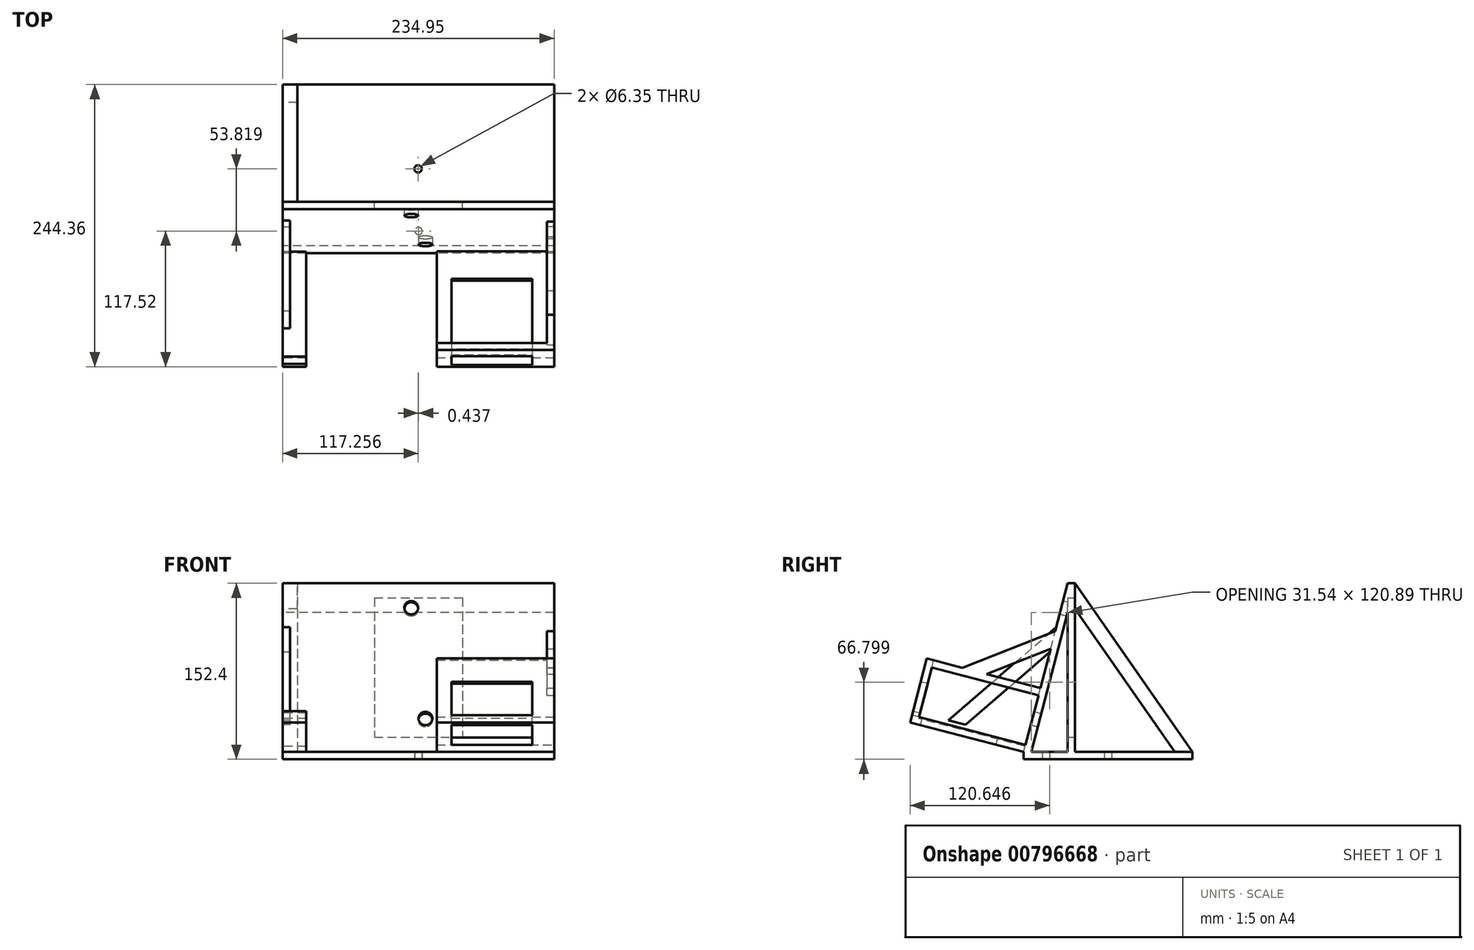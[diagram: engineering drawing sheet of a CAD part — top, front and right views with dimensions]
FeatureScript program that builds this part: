
annotation { "Feature Type Name" : "Feature", "Feature Type Description" : "" }
export const myFeature = defineFeature(function(context is Context, id is Id, definition is map)
    precondition{}
    {
        {
            var Q0;
            Q0=qCreatedBy(makeId("Right.planeOp"),FACE);
            var sketch = newSketch(context, id + "F0", { "sketchPlane" : qUnion([Q0])});
            skLineSegment(sketch, "E0.bottom", {"start": v(-30.3, 47.63) * mm, "end": v(14.14, 47.63) * mm, "construction": true});
            skLineSegment(sketch, "E0.top", {"start": v(-30.3, 41.28) * mm, "end": v(14.14, 41.28) * mm});
            skLineSegment(sketch, "E0.left", {"start": v(-30.3, 47.63) * mm, "end": v(-30.3, 41.28) * mm});
            skLineSegment(sketch, "E0.right", {"start": v(14.14, 47.63) * mm, "end": v(14.14, 41.28) * mm});
            skLineSegment(sketch, "E1.bottom", {"start": v(14.14, 47.63) * mm, "end": v(7.8, 47.63) * mm});
            skLineSegment(sketch, "E1.top", {"start": v(14.14, 193.68) * mm, "end": v(7.8, 193.68) * mm});
            skLineSegment(sketch, "E1.left", {"start": v(14.14, 47.63) * mm, "end": v(14.14, 193.68) * mm});
            skLineSegment(sketch, "E1.right", {"start": v(7.8, 47.63) * mm, "end": v(7.8, 193.68) * mm});
            skLineSegment(sketch, "E2.bottom", {"start": v(14.14, 41.28) * mm, "end": v(115.74, 41.28) * mm});
            skLineSegment(sketch, "E2.top", {"start": v(14.14, 47.63) * mm, "end": v(115.74, 47.63) * mm});
            skLineSegment(sketch, "E2.left", {"start": v(14.14, 41.28) * mm, "end": v(14.14, 47.63) * mm});
            skLineSegment(sketch, "E2.right", {"start": v(115.74, 41.28) * mm, "end": v(115.74, 47.63) * mm});
            skLineSegment(sketch, "E3", {"start": v(-30.3, 47.63) * mm, "end": v(7.8, 193.68) * mm});
            skLineSegment(sketch, "E4", {"start": v(-23.72, 47.63) * mm, "end": v(7.8, 168.45) * mm, "construction": true});
            skLineSegment(sketch, "E5", {"start": v(-17.69, 96) * mm, "end": v(-11.54, 94.4) * mm, "construction": true});
            skLineSegment(sketch, "E6", {"start": v(-23.72, 47.63) * mm, "end": v(7.8, 47.63) * mm, "construction": true});
            skLineSegment(sketch, "E7", {"start": v(7.8, 47.63) * mm, "end": v(7.8, 168.45) * mm, "construction": true});
            skLineSegment(sketch, "E8", {"start": v(115.74, 47.63) * mm, "end": v(115.74, 94.76) * mm, "construction": true});
            skSolve(sketch);
        }
        {
            var Q0;
            Q0=makeQuery(id+"F0.imprint","IMPRINT",FACE,{"disambiguationData":[TD([[makeQuery(id+"F0.imprint","IMPRINT",EDGE,{"derivedFrom":sQuery(id+"F0.wireOp",EDGE,"E0.top")}),1.0]])]});
            var Q1;
            {var subQ1=sQuery(id+"F0.wireOp",EDGE,"E1.bottom");Q1=makeQuery(id+"F0.imprint","IMPRINT",FACE,{"disambiguationData":[TD([[makeQuery(id+"F0.imprint","IMPRINT",EDGE,{"derivedFrom":subQ1}),-1.0]])]});}
            var Q2;
            {var subQ0=sQuery(id+"F0.wireOp",EDGE,"E3");Q2=makeQuery(id+"F0.imprint","IMPRINT",FACE,{"disambiguationData":[TD([[makeQuery(id+"F0.imprint","IMPRINT",EDGE,{"derivedFrom":subQ0}),-1.0]])]});}
            var Q3;
            Q3=makeQuery(id+"F0.imprint","IMPRINT",FACE,{"disambiguationData":[TD([[makeQuery(id+"F0.imprint","IMPRINT",EDGE,{"derivedFrom":sQuery(id+"F0.wireOp",EDGE,"E2.bottom")}),1.0]])]});
            extrude(context, id + "F1", {"entities" : qUnion([Q0, Q1, Q2, Q3]), "depth" : 228.6 * mm, "offsetDistance" : 25.4 * mm});
        }
        {
            var Q0;
            Q0=makeQuery(id+"F1.opExtrude","CAP_FACE",FACE,{"disambiguationData":[OSD([sQuery(id+"F0.wireOp",EDGE,"E0.bottom"),sQuery(id+"F0.wireOp",EDGE,"E0.top"),sQuery(id+"F0.wireOp",EDGE,"E0.left"),sQuery(id+"F0.wireOp",EDGE,"E1.top"),sQuery(id+"F0.wireOp",EDGE,"E1.left"),sQuery(id+"F0.wireOp",EDGE,"E1.right"),sQuery(id+"F0.wireOp",EDGE,"E2.bottom"),sQuery(id+"F0.wireOp",EDGE,"E2.top"),sQuery(id+"F0.wireOp",EDGE,"E2.right"),sQuery(id+"F0.wireOp",EDGE,"E3"),sQuery(id+"F0.wireOp",EDGE,"E4")])],"isStart":false});
            var sketch = newSketch(context, id + "F2", { "sketchPlane" : qUnion([Q0])});
            skLineSegment(sketch, "E9", {"start": v(-30.3, 47.63) * mm, "end": v(-128.62, 73.28) * mm});
            skLineSegment(sketch, "E10", {"start": v(-128.62, 73.28) * mm, "end": v(-114.19, 128.58) * mm});
            skLineSegment(sketch, "E11", {"start": v(-114.19, 128.58) * mm, "end": v(-15.88, 102.93) * mm, "construction": true});
            skLineSegment(sketch, "E12", {"start": v(-121.4, 100.93) * mm, "end": v(-115.26, 99.32) * mm, "construction": true});
            skLineSegment(sketch, "E13", {"start": v(-67.67, 116.44) * mm, "end": v(-69.28, 110.3) * mm, "construction": true});
            skLineSegment(sketch, "E14", {"start": v(-115.26, 99.32) * mm, "end": v(-109.65, 120.83) * mm});
            skLineSegment(sketch, "E15", {"start": v(-109.65, 120.83) * mm, "end": v(-69.28, 110.3) * mm});
            skLineSegment(sketch, "E16", {"start": v(-69.28, 110.3) * mm, "end": v(-17.48, 96.79) * mm});
            skLineSegment(sketch, "E17", {"start": v(-115.26, 99.32) * mm, "end": v(-122.47, 71.68) * mm});
            skLineSegment(sketch, "E18", {"start": v(-109.65, 120.83) * mm, "end": v(-108.05, 126.97) * mm});
            skLineSegment(sketch, "E19", {"start": v(-108.2, 67.95) * mm, "end": v(-106.6, 74.1) * mm, "construction": true});
            skLineSegment(sketch, "E20", {"start": v(-120.87, 77.82) * mm, "end": v(-106.6, 74.1) * mm});
            skLineSegment(sketch, "E21", {"start": v(-106.6, 74.1) * mm, "end": v(-28.7, 53.78) * mm});
            skLineSegment(sketch, "E22", {"start": v(-15.88, 102.93) * mm, "end": v(-17.48, 96.79) * mm});
            skLineSegment(sketch, "E23", {"start": v(-108.05, 126.97) * mm, "end": v(-15.88, 102.93) * mm});
            skLineSegment(sketch, "E24", {"start": v(-108.05, 126.97) * mm, "end": v(-114.19, 128.58) * mm});
            skLineSegment(sketch, "E25", {"start": v(-108.05, 126.97) * mm, "end": v(-83.47, 120.56) * mm, "construction": true});
            skLineSegment(sketch, "E26", {"start": v(-28.7, 53.78) * mm, "end": v(-3.06, 152.09) * mm, "construction": true});
            skLineSegment(sketch, "E27", {"start": v(-83.47, 120.56) * mm, "end": v(-3.06, 152.09) * mm});
            skLineSegment(sketch, "E28", {"start": v(-35.28, 139.46) * mm, "end": v(-30.64, 127.63) * mm, "construction": true});
            skLineSegment(sketch, "E29", {"start": v(-62.57, 115.11) * mm, "end": v(-30.64, 127.63) * mm});
            skLineSegment(sketch, "E30", {"start": v(-30.64, 127.63) * mm, "end": v(-7.02, 136.9) * mm});
            skSolve(sketch);
        }
        {
            var Q0;
            Q0=makeQuery(id+"F2.imprint","IMPRINT",FACE,{"disambiguationData":[TD([[makeQuery(id+"F2.imprint","IMPRINT",EDGE,{"derivedFrom":sQuery(id+"F2.wireOp",EDGE,"E15")}),1.0]])]});
            var sketch = newSketch(context, id + "F3", { "sketchPlane" : qUnion([Q0])});
            skSolve(sketch);
        }
        {
            var Q0;
            {var subQ1=sQuery(id+"F2.wireOp",EDGE,"E10");Q0=makeQuery(id+"F2.imprint","IMPRINT",FACE,{"disambiguationData":[TD([[makeQuery(id+"F2.imprint","IMPRINT",EDGE,{"derivedFrom":subQ1}),-1.0]])]});}
            var Q1;
            {var subQ1=sQuery(id+"F2.wireOp",EDGE,"E20");Q1=makeQuery(id+"F2.imprint","IMPRINT",FACE,{"disambiguationData":[TD([[makeQuery(id+"F2.imprint","IMPRINT",EDGE,{"derivedFrom":subQ1}),-1.0]])]});}
            extrude(context, id + "F4", {"entities" : qUnion([Q0, Q1]), "operationType" : NewBodyOperationType.ADD, "depth" : -101.6 * mm, "offsetDistance" : 25.4 * mm});
        }
        {
            var Q0;
            Q0 = qSketchRegion(id + "F3", true);
            var Q1;
            Q1=makeQuery(id+"F3.imprint","IMPRINT",FACE,{"disambiguationData":[TD([[makeQuery(id+"F3.imprint","IMPRINT",EDGE,{"derivedFrom":makeQuery(id+"F2.imprint","IMPRINT",EDGE,{"derivedFrom":sQuery(id+"F2.wireOp",EDGE,"E15")})}),1.0]])]});
            extrude(context, id + "F5", {"entities" : qUnion([Q0, Q1]), "operationType" : NewBodyOperationType.ADD, "depth" : -6.35 * mm, "offsetDistance" : 25.4 * mm});
        }
        {
            var Q0;
            Q0=makeQuery(id+"F4.opExtrude","SWEPT_FACE",FACE,{"disambiguationData":[OSD([sQuery(id+"F2.wireOp",EDGE,"E20"),sQuery(id+"F2.wireOp",EDGE,"E21")])]});
            var sketch = newSketch(context, id + "F6", { "sketchPlane" : qUnion([Q0])});
            skPoint(sketch, "E31.oppositeSnap0", {"position": v(127, -88.97) * mm});
            skLineSegment(sketch, "E32.bottom", {"start": v(139.7, -65.96) * mm, "end": v(209.55, -65.96) * mm});
            skLineSegment(sketch, "E32.top", {"start": v(139.7, -133.75) * mm, "end": v(209.55, -133.75) * mm});
            skLineSegment(sketch, "E32.left", {"start": v(139.7, -65.96) * mm, "end": v(139.7, -133.75) * mm});
            skLineSegment(sketch, "E32.right", {"start": v(209.55, -65.96) * mm, "end": v(209.55, -133.75) * mm});
            skLineSegment(sketch, "E33", {"start": v(228.6, -118.83) * mm, "end": v(209.55, -118.83) * mm, "construction": true});
            skLineSegment(sketch, "E34", {"start": v(127, -112.64) * mm, "end": v(139.7, -112.64) * mm, "construction": true});
            skLineSegment(sketch, "E35", {"start": v(166.89, -136.6) * mm, "end": v(166.89, -133.75) * mm, "construction": true});
            skSolve(sketch);
        }
        {
            var Q0;
            Q0=makeQuery(id+"F4.opExtrude","SWEPT_FACE",FACE,{"disambiguationData":[OSD([sQuery(id+"F2.wireOp",EDGE,"E10")])]});
            var sketch = newSketch(context, id + "F7", { "sketchPlane" : qUnion([Q0])});
            skLineSegment(sketch, "E36.bottom", {"start": v(139.7, 44.79) * mm, "end": v(209.55, 44.79) * mm});
            skLineSegment(sketch, "E36.top", {"start": v(139.7, 74.6) * mm, "end": v(209.55, 74.6) * mm});
            skLineSegment(sketch, "E36.left", {"start": v(139.7, 44.79) * mm, "end": v(139.7, 74.6) * mm});
            skLineSegment(sketch, "E36.right", {"start": v(209.55, 44.79) * mm, "end": v(209.55, 74.6) * mm});
            skLineSegment(sketch, "E37", {"start": v(127, 55.7) * mm, "end": v(139.7, 55.7) * mm, "construction": true});
            skLineSegment(sketch, "E38", {"start": v(228.6, 44.88) * mm, "end": v(209.55, 44.88) * mm, "construction": true});
            skLineSegment(sketch, "E39", {"start": v(147.27, 74.6) * mm, "end": v(147.27, 95.59) * mm, "construction": true});
            skLineSegment(sketch, "E40", {"start": v(180.91, 38.44) * mm, "end": v(180.91, 44.79) * mm, "construction": true});
            skSolve(sketch);
        }
        {
            var Q0;
            Q0=makeQuery(id+"F7.imprint","IMPRINT",FACE,{"disambiguationData":[TD([[makeQuery(id+"F7.imprint","IMPRINT",EDGE,{"derivedFrom":sQuery(id+"F7.wireOp",EDGE,"E36.bottom")}),1.0]])]});
            extrude(context, id + "F8", {"entities" : qUnion([Q0]), "operationType" : NewBodyOperationType.REMOVE, "endBound" : BoundingType.UP_TO_NEXT, "oppositeDirection" : true, "depth" : 25.4 * mm, "offsetDistance" : 25.4 * mm});
        }
        {
            var Q0;
            Q0=makeQuery(id+"F6.imprint","IMPRINT",FACE,{"disambiguationData":[TD([[makeQuery(id+"F6.imprint","IMPRINT",EDGE,{"derivedFrom":sQuery(id+"F6.wireOp",EDGE,"E32.bottom")}),-1.0]])]});
            extrude(context, id + "F9", {"entities" : qUnion([Q0]), "operationType" : NewBodyOperationType.REMOVE, "endBound" : BoundingType.UP_TO_NEXT, "oppositeDirection" : true, "depth" : 25.4 * mm, "offsetDistance" : 25.4 * mm});
        }
        {
            var Q0;
            {var subQ1=sQuery(id+"F2.wireOp",EDGE,"E27");Q0=makeQuery(id+"F2.imprint","IMPRINT",FACE,{"disambiguationData":[TD([[makeQuery(id+"F2.imprint","IMPRINT",EDGE,{"derivedFrom":subQ1}),-1.0]])]});}
            var Q1;
            {var subQ0=sQuery(id+"F2.wireOp",EDGE,"E18");var subQ1=sQuery(id+"F0.wireOp",EDGE,"E3");Q1=makeQuery(id+"F5.boolean.opBoolean","MERGE",FACE,{"derivedFrom":[makeQuery(id+"F4.boolean.opBoolean","MERGE",FACE,{"derivedFrom":[makeQuery(id+"F1.opExtrude","CAP_FACE",FACE,{"disambiguationData":[OSD([sQuery(id+"F0.wireOp",EDGE,"E0.top"),sQuery(id+"F0.wireOp",EDGE,"E0.left"),sQuery(id+"F0.wireOp",EDGE,"E1.top"),sQuery(id+"F0.wireOp",EDGE,"E1.left"),sQuery(id+"F0.wireOp",EDGE,"E2.bottom"),sQuery(id+"F0.wireOp",EDGE,"E2.top"),sQuery(id+"F0.wireOp",EDGE,"E2.right"),subQ1])],"isStart":false}),makeQuery(id+"F4.opExtrude","CAP_FACE",FACE,{"disambiguationData":[OSD([subQ1,sQuery(id+"F2.wireOp",EDGE,"E9"),sQuery(id+"F2.wireOp",EDGE,"E10"),sQuery(id+"F2.wireOp",EDGE,"E14"),sQuery(id+"F2.wireOp",EDGE,"E17"),sQuery(id+"F2.wireOp",EDGE,"E20"),sQuery(id+"F2.wireOp",EDGE,"E21"),subQ0,sQuery(id+"F2.wireOp",EDGE,"E24")])],"isStart":true})]}),makeQuery(id+"F5.opExtrude","CAP_FACE",FACE,{"disambiguationData":[OSD([sQuery(id+"F2.wireOp",EDGE,"E15"),sQuery(id+"F2.wireOp",EDGE,"E16"),sQuery(id+"F2.wireOp",EDGE,"E22"),subQ0,sQuery(id+"F2.wireOp",EDGE,"E23")])],"isStart":true})]});}
            var Q2;
            Q2 = qSketchRegion(id + "F0", true);
            extrude(context, id + "F10", {"entities" : qUnion([Q0, Q1, Q2]), "operationType" : NewBodyOperationType.ADD, "depth" : -6.35 * mm, "offsetDistance" : 25.4 * mm});
        }
        {
            var Q0;
            Q0=makeQuery(id+"F10.opExtrude","CAP_FACE",FACE,{"disambiguationData":[OSD([sQuery(id+"F0.wireOp",EDGE,"E0.top"),sQuery(id+"F0.wireOp",EDGE,"E0.left"),sQuery(id+"F0.wireOp",EDGE,"E1.top"),sQuery(id+"F0.wireOp",EDGE,"E1.left"),sQuery(id+"F0.wireOp",EDGE,"E2.bottom"),sQuery(id+"F0.wireOp",EDGE,"E2.top"),sQuery(id+"F0.wireOp",EDGE,"E2.right"),sQuery(id+"F0.wireOp",EDGE,"E3")])],"isStart":false});
            var sketch = newSketch(context, id + "F11", { "sketchPlane" : qUnion([Q0])});
            skLineSegment(sketch, "E41", {"start": v(4.15, 41.28) * mm, "end": v(4.15, 47.63) * mm, "construction": true});
            skLineSegment(sketch, "E42", {"start": v(24.74, 68.97) * mm, "end": v(18.6, 67.37) * mm, "construction": true});
            skLineSegment(sketch, "E43", {"start": v(-14.14, 47.63) * mm, "end": v(27.4, 47.63) * mm, "construction": true});
            skLineSegment(sketch, "E44", {"start": v(-14.14, 73.77) * mm, "end": v(-7.8, 73.77) * mm, "construction": true});
            skLineSegment(sketch, "E45", {"start": v(18.6, 67.37) * mm, "end": v(23.74, 47.63) * mm});
            skLineSegment(sketch, "E46", {"start": v(-7.8, 73.77) * mm, "end": v(-7.8, 47.63) * mm});
            skLineSegment(sketch, "E47", {"start": v(23.74, 47.63) * mm, "end": v(-7.8, 47.63) * mm});
            skLineSegment(sketch, "E48", {"start": v(-7.8, 73.77) * mm, "end": v(-7.8, 168.53) * mm});
            skLineSegment(sketch, "E49", {"start": v(18.6, 67.37) * mm, "end": v(-7.8, 168.53) * mm});
            skSolve(sketch);
        }
        {
            var Q0;
            Q0=makeQuery(id+"F11.imprint","IMPRINT",FACE,{"disambiguationData":[TD([[makeQuery(id+"F11.imprint","IMPRINT",EDGE,{"derivedFrom":sQuery(id+"F11.wireOp",EDGE,"E45")}),-1.0]])]});
            extrude(context, id + "F12", {"entities" : qUnion([Q0]), "operationType" : NewBodyOperationType.REMOVE, "endBound" : BoundingType.UP_TO_NEXT, "oppositeDirection" : true, "depth" : 25.4 * mm, "offsetDistance" : 25.4 * mm});
        }
        {
            var Q0;
            {var subQ0=sQuery(id+"F0.wireOp",EDGE,"E2.bottom");var subQ1=sQuery(id+"F0.wireOp",EDGE,"E0.top");Q0=makeQuery(id+"F10.boolean.opBoolean","MERGE",FACE,{"derivedFrom":[makeQuery(id+"F1.opExtrude","SWEPT_FACE",FACE,{"disambiguationData":[OSD([subQ1,subQ0])]}),makeQuery(id+"F10.opExtrude","SWEPT_FACE",FACE,{"disambiguationData":[OSD([subQ1,subQ0]),TDD([makeQuery(id+"F0.imprint","IMPRINT",EDGE,{"derivedFrom":subQ1}),makeQuery(id+"F0.imprint","IMPRINT",EDGE,{"derivedFrom":subQ0})])]})]});}
            var sketch = newSketch(context, id + "F13", { "sketchPlane" : qUnion([Q0])});
            skLineSegment(sketch, "E50", {"start": v(174.81, 30.3) * mm, "end": v(174.81, -7.8) * mm, "construction": true});
            skLineSegment(sketch, "E51", {"start": v(174.81, -7.8) * mm, "end": v(228.6, -7.8) * mm, "construction": true});
            skLineSegment(sketch, "E52", {"start": v(174.81, -7.8) * mm, "end": v(0, -7.8) * mm, "construction": true});
            skLineSegment(sketch, "E53", {"start": v(110.9, 30.3) * mm, "end": v(110.9, 11.41) * mm, "construction": true});
            skLineSegment(sketch, "E54", {"start": v(110.9, 11.1) * mm, "end": v(110.9, -7.8) * mm});
            skLineSegment(sketch, "E55", {"start": v(110.9, 11.41) * mm, "end": v(228.6, 11.41) * mm, "construction": true});
            skLineSegment(sketch, "E56", {"start": v(111.34, 11.1) * mm, "end": v(-6.35, 11.1) * mm, "construction": true});
            skCircle(sketch, "E57", {"center": v(111.34, 11.1) * mm, "radius": 3.18 * mm});
            skLineSegment(sketch, "E58", {"start": v(-6.35, -42.72) * mm, "end": v(110.9, -42.72) * mm, "construction": true});
            skLineSegment(sketch, "E59", {"start": v(110.9, -42.72) * mm, "end": v(228.6, -42.72) * mm, "construction": true});
            skLineSegment(sketch, "E60", {"start": v(110.9, -115.74) * mm, "end": v(110.9, -42.72) * mm, "construction": true});
            skLineSegment(sketch, "E61", {"start": v(110.9, 30.3) * mm, "end": v(110.9, -42.72) * mm, "construction": true});
            skCircle(sketch, "E62", {"center": v(110.9, -42.72) * mm, "radius": 3.18 * mm});
            skSolve(sketch);
        }
        {
            var Q0;
            Q0 = qSketchRegion(id + "F13", true);
            extrude(context, id + "F14", {"entities" : qUnion([Q0]), "operationType" : NewBodyOperationType.REMOVE, "endBound" : BoundingType.UP_TO_NEXT, "oppositeDirection" : true, "depth" : 25.4 * mm, "offsetDistance" : 25.4 * mm});
        }
        {
            var Q0;
            Q0=makeQuery(id+"F10.opExtrude","CAP_FACE",FACE,{"disambiguationData":[OSD([sQuery(id+"F0.wireOp",EDGE,"E0.top"),sQuery(id+"F0.wireOp",EDGE,"E0.left"),sQuery(id+"F0.wireOp",EDGE,"E1.top"),sQuery(id+"F0.wireOp",EDGE,"E1.left"),sQuery(id+"F0.wireOp",EDGE,"E2.bottom"),sQuery(id+"F0.wireOp",EDGE,"E2.top"),sQuery(id+"F0.wireOp",EDGE,"E2.right"),sQuery(id+"F0.wireOp",EDGE,"E3")])],"isStart":false});
            var sketch = newSketch(context, id + "F15", { "sketchPlane" : qUnion([Q0])});
            skLineSegment(sketch, "E63", {"start": v(30.3, 47.63) * mm, "end": v(128.62, 73.28) * mm});
            skLineSegment(sketch, "E64", {"start": v(128.62, 73.28) * mm, "end": v(126.05, 83.1) * mm});
            skLineSegment(sketch, "E65", {"start": v(126.05, 83.1) * mm, "end": v(27.74, 57.46) * mm});
            skLineSegment(sketch, "E66", {"start": v(27.74, 57.46) * mm, "end": v(30.3, 47.63) * mm});
            skLineSegment(sketch, "E67", {"start": v(127.33, 78.2) * mm, "end": v(121.19, 76.6) * mm, "construction": true});
            skLineSegment(sketch, "E68", {"start": v(121.19, 76.6) * mm, "end": v(119.9, 81.5) * mm, "construction": true});
            skLineSegment(sketch, "E69", {"start": v(119.9, 81.5) * mm, "end": v(120.87, 77.82) * mm, "construction": true});
            skLineSegment(sketch, "E70", {"start": v(119.9, 81.5) * mm, "end": v(120.87, 77.82) * mm});
            skLineSegment(sketch, "E71", {"start": v(119.9, 81.5) * mm, "end": v(121.19, 76.6) * mm});
            skLineSegment(sketch, "E72", {"start": v(29.02, 52.55) * mm, "end": v(27.74, 57.46) * mm});
            skLineSegment(sketch, "E73", {"start": v(29.02, 52.55) * mm, "end": v(121.19, 76.6) * mm});
            skLineSegment(sketch, "E74", {"start": v(119.9, 81.5) * mm, "end": v(95.33, 75.1) * mm, "construction": true});
            skLineSegment(sketch, "E75", {"start": v(27.74, 57.46) * mm, "end": v(2.1, 155.77) * mm, "construction": true});
            skLineSegment(sketch, "E76", {"start": v(95.33, 75.1) * mm, "end": v(2.1, 155.77) * mm});
            skLineSegment(sketch, "E77", {"start": v(51.68, 112.87) * mm, "end": v(43.37, 103.26) * mm, "construction": true});
            skLineSegment(sketch, "E78", {"start": v(80.42, 71.2) * mm, "end": v(43.37, 103.26) * mm});
            skLineSegment(sketch, "E79", {"start": v(43.37, 103.26) * mm, "end": v(7.75, 134.08) * mm});
            skLineSegment(sketch, "E80", {"start": v(95.33, 75.1) * mm, "end": v(119.9, 81.5) * mm});
            skLineSegment(sketch, "E81", {"start": v(121.19, 76.6) * mm, "end": v(29.02, 52.55) * mm});
            skLineSegment(sketch, "E82", {"start": v(27.74, 57.46) * mm, "end": v(80.42, 71.2) * mm});
            skLineSegment(sketch, "E83", {"start": v(80.42, 71.2) * mm, "end": v(95.33, 75.1) * mm});
            skSolve(sketch);
        }
        {
            var Q0;
            Q0=makeQuery(id+"F15.imprint","IMPRINT",FACE,{"disambiguationData":[TD([[makeQuery(id+"F15.imprint","IMPRINT",EDGE,{"derivedFrom":sQuery(id+"F15.wireOp",EDGE,"E63")}),1.0]])]});
            extrude(context, id + "F16", {"entities" : qUnion([Q0]), "operationType" : NewBodyOperationType.ADD, "oppositeDirection" : true, "depth" : 20.32 * mm, "offsetDistance" : 25.4 * mm});
        }
        {
            var Q0;
            Q0=makeQuery(id+"F15.imprint","IMPRINT",FACE,{"disambiguationData":[TD([[makeQuery(id+"F15.imprint","IMPRINT",EDGE,{"derivedFrom":sQuery(id+"F15.wireOp",EDGE,"E72")}),-1.0]])]});
            var Q1;
            {var subQ1=sQuery(id+"F15.wireOp",EDGE,"E76");Q1=makeQuery(id+"F15.imprint","IMPRINT",FACE,{"disambiguationData":[TD([[makeQuery(id+"F15.imprint","IMPRINT",EDGE,{"derivedFrom":subQ1}),1.0]])]});}
            extrude(context, id + "F17", {"entities" : qUnion([Q0, Q1]), "operationType" : NewBodyOperationType.ADD, "oppositeDirection" : true, "depth" : 6.35 * mm, "offsetDistance" : 25.4 * mm});
        }
        {
            var Q0;
            {var subQ0=sQuery(id+"F0.wireOp",EDGE,"E3");Q0=makeQuery(id+"F10.boolean.opBoolean","MERGE",FACE,{"derivedFrom":[makeQuery(id+"F1.opExtrude","SWEPT_FACE",FACE,{"disambiguationData":[OSD([subQ0])]}),makeQuery(id+"F10.opExtrude","SWEPT_FACE",FACE,{"disambiguationData":[OSD([subQ0]),TDD([makeQuery(id+"F0.imprint","IMPRINT",EDGE,{"derivedFrom":subQ0})])]})]});}
            var sketch = newSketch(context, id + "F18", { "sketchPlane" : qUnion([Q0])});
            skLineSegment(sketch, "E84", {"start": v(117.25, 38.44) * mm, "end": v(117.25, 68.44) * mm, "construction": true});
            skLineSegment(sketch, "E85", {"start": v(117.25, 68.44) * mm, "end": v(222.25, 68.44) * mm, "construction": true});
            skLineSegment(sketch, "E86", {"start": v(222.25, 68.44) * mm, "end": v(228.6, 68.44) * mm, "construction": true});
            skCircle(sketch, "E87", {"center": v(117.25, 68.44) * mm, "radius": 6 * mm});
            skLineSegment(sketch, "E88", {"start": v(105, 189.38) * mm, "end": v(105, 167.56) * mm, "construction": true});
            skLineSegment(sketch, "E89", {"start": v(105, 167.56) * mm, "end": v(0, 167.56) * mm, "construction": true});
            skLineSegment(sketch, "E90", {"start": v(0, 167.56) * mm, "end": v(-6.35, 167.56) * mm, "construction": true});
            skCircle(sketch, "E91", {"center": v(105, 167.56) * mm, "radius": 6 * mm});
            skSolve(sketch);
        }
        {
            var Q0;
            {var subQ0=sQuery(id+"F0.wireOp",EDGE,"E1.left");Q0=makeQuery(id+"F10.boolean.opBoolean","MERGE",FACE,{"derivedFrom":[makeQuery(id+"F1.opExtrude","SWEPT_FACE",FACE,{"disambiguationData":[OSD([subQ0])]}),makeQuery(id+"F10.opExtrude","SWEPT_FACE",FACE,{"disambiguationData":[OSD([subQ0]),TDD([makeQuery(id+"F0.imprint","IMPRINT",EDGE,{"derivedFrom":subQ0})])]})]});}
            var sketch = newSketch(context, id + "F19", { "sketchPlane" : qUnion([Q0])});
            skLineSegment(sketch, "E92.bottom", {"start": v(-73.03, 180.98) * mm, "end": v(-149.22, 180.98) * mm});
            skLineSegment(sketch, "E92.top", {"start": v(-73.03, 60.33) * mm, "end": v(-149.22, 60.33) * mm});
            skLineSegment(sketch, "E92.left", {"start": v(-73.03, 180.98) * mm, "end": v(-73.03, 60.33) * mm});
            skLineSegment(sketch, "E92.right", {"start": v(-149.22, 180.98) * mm, "end": v(-149.22, 60.33) * mm});
            skLineSegment(sketch, "E93", {"start": v(-114.16, 60.33) * mm, "end": v(-114.16, 47.63) * mm, "construction": true});
            skPoint(sketch, "E93.endSnap0", {"position": v(-111.13, 47.63) * mm});
            skLineSegment(sketch, "E94", {"start": v(-114.16, 180.98) * mm, "end": v(-114.16, 193.68) * mm});
            skLineSegment(sketch, "E95", {"start": v(-149.23, 126.85) * mm, "end": v(-228.6, 126.85) * mm});
            skLineSegment(sketch, "E96", {"start": v(-73.03, 122.8) * mm, "end": v(6.35, 122.8) * mm});
            skSolve(sketch);
        }
        {
            var Q0;
            {var subQ4=sQuery(id+"F19.wireOp",EDGE,"E92.top");Q0=makeQuery(id+"F19.imprint","IMPRINT",FACE,{"disambiguationData":[TD([[makeQuery(id+"F19.imprint","IMPRINT",EDGE,{"derivedFrom":subQ4}),-1.0]])]});}
            extrude(context, id + "F20", {"entities" : qUnion([Q0]), "operationType" : NewBodyOperationType.REMOVE, "oppositeDirection" : true, "depth" : 6.35 * mm, "offsetDistance" : 25.4 * mm});
        }
        {
            var Q0;
            Q0=makeQuery(id+"F18.imprint","IMPRINT",FACE,{"disambiguationData":[TD([[makeQuery(id+"F18.imprint","IMPRINT",EDGE,{"derivedFrom":sQuery(id+"F18.wireOp",EDGE,"E87")}),1.0]])]});
            var Q1;
            Q1=makeQuery(id+"F18.imprint","IMPRINT",FACE,{"disambiguationData":[TD([[makeQuery(id+"F18.imprint","IMPRINT",EDGE,{"derivedFrom":sQuery(id+"F18.wireOp",EDGE,"E91")}),1.0]])]});
            extrude(context, id + "F21", {"entities" : qUnion([Q0, Q1]), "operationType" : NewBodyOperationType.REMOVE, "oppositeDirection" : true, "depth" : 12.7 * mm, "offsetDistance" : 25.4 * mm});
        }
        {
            var Q0;
            {var subQ0=sQuery(id+"F15.wireOp",EDGE,"E81");var subQ1=sQuery(id+"F15.wireOp",EDGE,"E71");var subQ2=sQuery(id+"F0.wireOp",EDGE,"E3");Q0=makeQuery(id+"F17.boolean.opBoolean","MERGE",FACE,{"derivedFrom":[makeQuery(id+"F16.boolean.opBoolean","MERGE",FACE,{"derivedFrom":[makeQuery(id+"F10.opExtrude","CAP_FACE",FACE,{"disambiguationData":[OSD([sQuery(id+"F0.wireOp",EDGE,"E0.top"),sQuery(id+"F0.wireOp",EDGE,"E0.left"),sQuery(id+"F0.wireOp",EDGE,"E1.top"),sQuery(id+"F0.wireOp",EDGE,"E1.left"),sQuery(id+"F0.wireOp",EDGE,"E2.bottom"),sQuery(id+"F0.wireOp",EDGE,"E2.top"),sQuery(id+"F0.wireOp",EDGE,"E2.right"),subQ2])],"isStart":false}),makeQuery(id+"F16.opExtrude","CAP_FACE",FACE,{"disambiguationData":[OSD([sQuery(id+"F15.wireOp",EDGE,"E63"),sQuery(id+"F15.wireOp",EDGE,"E64"),sQuery(id+"F15.wireOp",EDGE,"E65"),sQuery(id+"F15.wireOp",EDGE,"E66"),subQ1,subQ0])],"isStart":true})]}),makeQuery(id+"F17.opExtrude","CAP_FACE",FACE,{"disambiguationData":[OSD([subQ2,subQ1,sQuery(id+"F15.wireOp",EDGE,"E72"),sQuery(id+"F15.wireOp",EDGE,"E76"),sQuery(id+"F15.wireOp",EDGE,"E78"),sQuery(id+"F15.wireOp",EDGE,"E79"),sQuery(id+"F15.wireOp",EDGE,"E80"),subQ0,sQuery(id+"F15.wireOp",EDGE,"E82")])],"isStart":true})]});}
            var sketch = newSketch(context, id + "F22", { "sketchPlane" : qUnion([Q0])});
            skLineSegment(sketch, "E97", {"start": v(-14.14, 193.68) * mm, "end": v(-115.74, 47.63) * mm});
            skLineSegment(sketch, "E98", {"start": v(-94.82, 77.71) * mm, "end": v(-84.4, 70.46) * mm, "construction": true});
            skLineSegment(sketch, "E99", {"start": v(-84.4, 70.46) * mm, "end": v(-100.27, 47.63) * mm});
            skLineSegment(sketch, "E100", {"start": v(-84.4, 70.46) * mm, "end": v(-14.14, 171.44) * mm});
            skSolve(sketch);
        }
        {
            var Q0;
            {var subQ0=sQuery(id+"F22.wireOp",EDGE,"E97");Q0=makeQuery(id+"F22.imprint","IMPRINT",FACE,{"disambiguationData":[TD([[makeQuery(id+"F22.imprint","IMPRINT",EDGE,{"derivedFrom":subQ0}),1.0]])]});}
            extrude(context, id + "F23", {"entities" : qUnion([Q0]), "operationType" : NewBodyOperationType.ADD, "oppositeDirection" : true, "depth" : 12.7 * mm, "offsetDistance" : 25.4 * mm});
        }
    });
